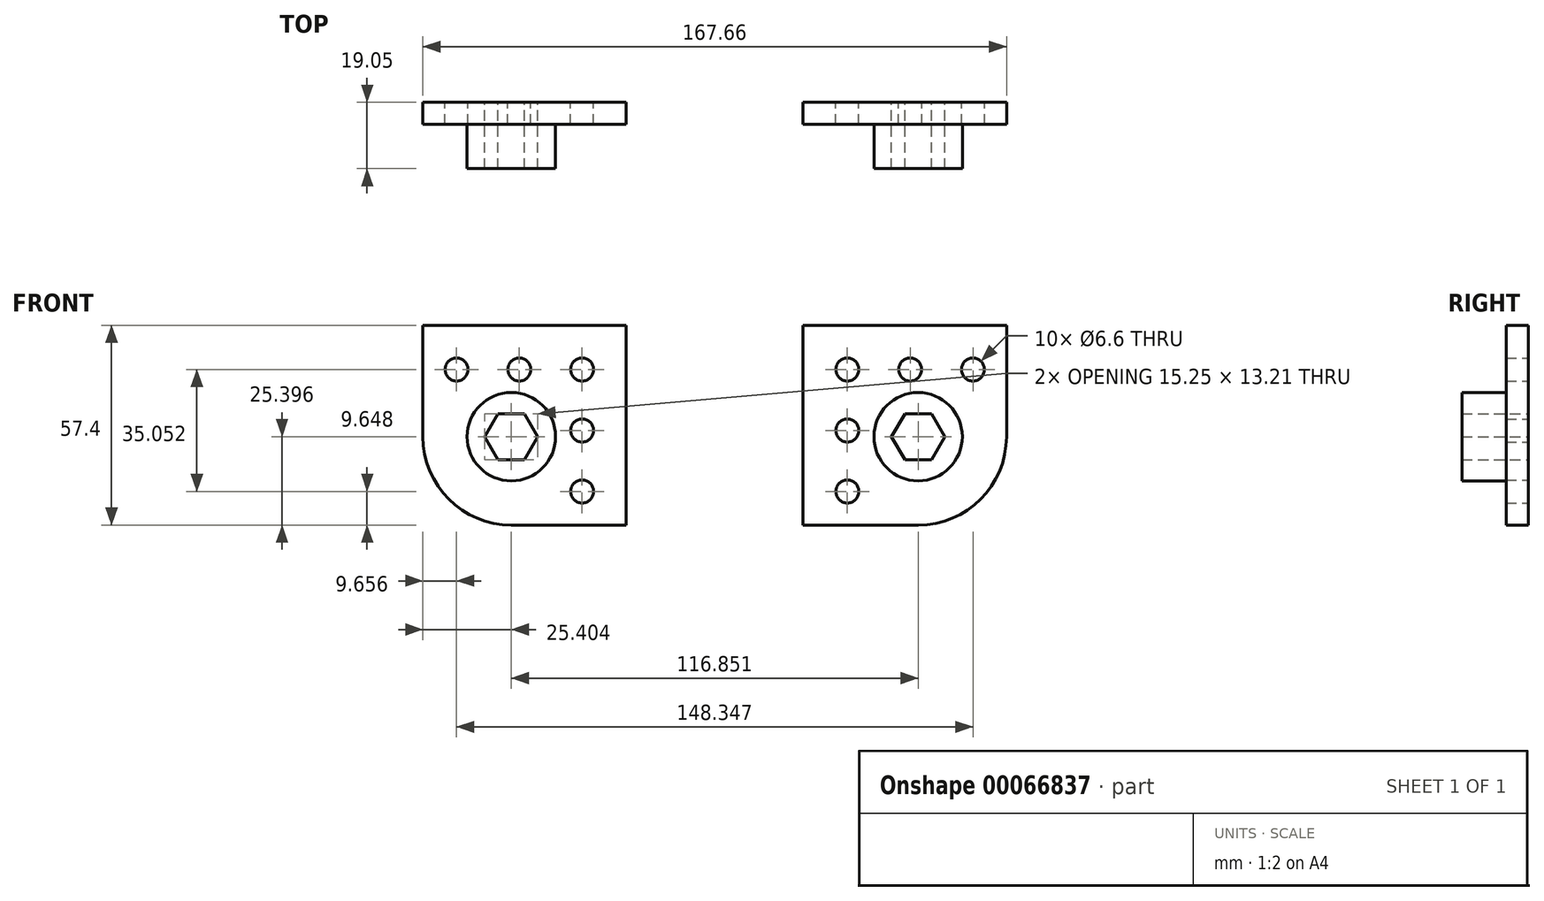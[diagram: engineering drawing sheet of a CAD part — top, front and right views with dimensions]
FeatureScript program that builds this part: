
annotation { "Feature Type Name" : "Feature", "Feature Type Description" : "" }
export const myFeature = defineFeature(function(context is Context, id is Id, definition is map)
    precondition{}
    {
        {
            var Q0;
            Q0=qCreatedBy(makeId("Front.planeOp"),FACE);
            var sketch = newSketch(context, id + "F0", { "sketchPlane" : qUnion([Q0])});
            skLineSegment(sketch, "E0.top", {"start": v(0, 25.4) * mm, "end": v(-58.43, 25.4) * mm});
            skLineSegment(sketch, "E0.left", {"start": v(0, 0) * mm, "end": v(0, 25.4) * mm});
            skLineSegment(sketch, "E1.left", {"start": v(0, 0) * mm, "end": v(0, -32) * mm});
            skCircle(sketch, "E2.cCircle", {"center": v(-33.03, -6.6) * mm, "radius": 6.6 * mm, "construction": true});
            skLineSegment(sketch, "E2.0", {"start": v(-36.84, 0) * mm, "end": v(-29.21, 0) * mm});
            skLineSegment(sketch, "E2.1", {"start": v(-29.21, 0) * mm, "end": v(-25.4, -6.6) * mm});
            skLineSegment(sketch, "E2.2", {"start": v(-25.4, -6.6) * mm, "end": v(-29.21, -13.2) * mm});
            skLineSegment(sketch, "E2.3", {"start": v(-29.21, -13.2) * mm, "end": v(-36.84, -13.2) * mm});
            skLineSegment(sketch, "E2.4", {"start": v(-36.84, -13.2) * mm, "end": v(-40.65, -6.6) * mm});
            skLineSegment(sketch, "E2.5", {"start": v(-40.65, -6.6) * mm, "end": v(-36.84, 0) * mm});
            skPoint(sketch, "E2.0.midPoint", {"position": v(-33.03, 0) * mm});
            skCircle(sketch, "E3", {"center": v(-33.03, -6.6) * mm, "radius": 25.4 * mm});
            skCircle(sketch, "E4", {"center": v(-33.03, -6.6) * mm, "radius": 12.7 * mm});
            skLineSegment(sketch, "E5", {"start": v(-33.03, -6.6) * mm, "end": v(-66.73, -6.6) * mm, "construction": true});
            skLineSegment(sketch, "E6", {"start": v(-58.43, -6.6) * mm, "end": v(-58.43, 25.4) * mm});
            skLineSegment(sketch, "E7", {"start": v(-33.03, -6.6) * mm, "end": v(-33.03, -32) * mm, "construction": true});
            skLineSegment(sketch, "E8", {"start": v(-33.03, -32) * mm, "end": v(0, -32) * mm});
            skCircle(sketch, "E9", {"center": v(-12.7, 12.7) * mm, "radius": 3.3 * mm});
            skCircle(sketch, "E10", {"center": v(-30.74, 12.7) * mm, "radius": 3.3 * mm});
            skCircle(sketch, "E11", {"center": v(-48.77, 12.7) * mm, "radius": 3.3 * mm});
            skLineSegment(sketch, "E12", {"start": v(-48.77, 12.7) * mm, "end": v(-12.7, 12.7) * mm, "construction": true});
            skLineSegment(sketch, "E13", {"start": v(-30.74, 12.7) * mm, "end": v(-30.74, 35.67) * mm, "construction": true});
            skCircle(sketch, "E14", {"center": v(-12.7, -4.83) * mm, "radius": 3.3 * mm});
            skCircle(sketch, "E15", {"center": v(-12.7, -22.35) * mm, "radius": 3.3 * mm});
            skLineSegment(sketch, "E16", {"start": v(-12.7, 12.7) * mm, "end": v(-12.7, -22.35) * mm, "construction": true});
            skLineSegment(sketch, "E17", {"start": v(-12.7, -4.83) * mm, "end": v(15.11, -4.83) * mm, "construction": true});
            skSolve(sketch);
        }
        {
            var Q0;
            Q0 = qSketchRegion(id + "F0", true);
            var Q1;
            {var subQ0=sQuery(id+"F0.wireOp",EDGE,"E4");var subQ1=sQuery(id+"F0.wireOp",EDGE,"E0.bottom");var subQ2=makeQuery(id+"F0.imprint","INTERSECT",VERTEX,{"derivedFrom":[subQ1,subQ0]});Q1=makeQuery(id+"F0.imprint","IMPRINT",FACE,{"disambiguationData":[TD([[makeQuery(id+"F0.imprint","IMPRINT",EDGE,{"disambiguationData":[TD([[subQ2,-1.0]])],"derivedFrom":subQ1}),-1.0]])]});}
            var Q2;
            {var subQ0=sQuery(id+"F0.wireOp",EDGE,"E3");var subQ1=sQuery(id+"F0.wireOp",EDGE,"E1.bottom");var subQ2=makeQuery(id+"F0.imprint","INTERSECT",VERTEX,{"derivedFrom":[subQ1,subQ0]});Q2=makeQuery(id+"F0.imprint","IMPRINT",FACE,{"disambiguationData":[TD([[makeQuery(id+"F0.imprint","IMPRINT",EDGE,{"disambiguationData":[TD([[subQ2,-1.0]])],"derivedFrom":subQ1}),1.0]])]});}
            extrude(context, id + "F1", {"entities" : qUnion([Q0, Q1, Q2]), "depth" : 6.35 * mm});
        }
        {
            var Q0;
            Q0=makeQuery(id+"F0.imprint","IMPRINT",FACE,{"disambiguationData":[TD([[makeQuery(id+"F0.imprint","IMPRINT",EDGE,{"derivedFrom":sQuery(id+"F0.wireOp",EDGE,"E2.0")}),1.0]])]});
            extrude(context, id + "F2", {"entities" : qUnion([Q0]), "operationType" : NewBodyOperationType.ADD, "depth" : 19.05 * mm});
        }
        {
            var Q0;
            Q0=qCreatedBy(makeId("Right.planeOp"),FACE);
            cPlane(context, id + "F3", {"entities" : qUnion([Q0]), "cplaneType" : CPlaneType.OFFSET, "offset" : 25.4 * mm, "width" : 152.4 * mm, "height" : 152.4 * mm});
        }
        {
            var Q0;
            Q0=makeQuery(id+"F1.opExtrude","SWEPT_BODY",BODY,{"disambiguationData":[OSD([sQuery(id+"F0.wireOp",EDGE,"E0.top"),sQuery(id+"F0.wireOp",EDGE,"E0.left"),sQuery(id+"F0.wireOp",EDGE,"E1.left"),sQuery(id+"F0.wireOp",EDGE,"E3"),sQuery(id+"F0.wireOp",EDGE,"E4"),sQuery(id+"F0.wireOp",EDGE,"E6"),sQuery(id+"F0.wireOp",EDGE,"E8"),sQuery(id+"F0.wireOp",EDGE,"E9"),sQuery(id+"F0.wireOp",EDGE,"E10"),sQuery(id+"F0.wireOp",EDGE,"E11"),sQuery(id+"F0.wireOp",EDGE,"E14"),sQuery(id+"F0.wireOp",EDGE,"E15")])]});
            var Q1;
            Q1=qCreatedBy(id+"F3.planeOp",FACE);
            mirror(context, id + "F4", {"entities" : qUnion([Q0]), "mirrorPlane" : qUnion([Q1])});
        }
    });
